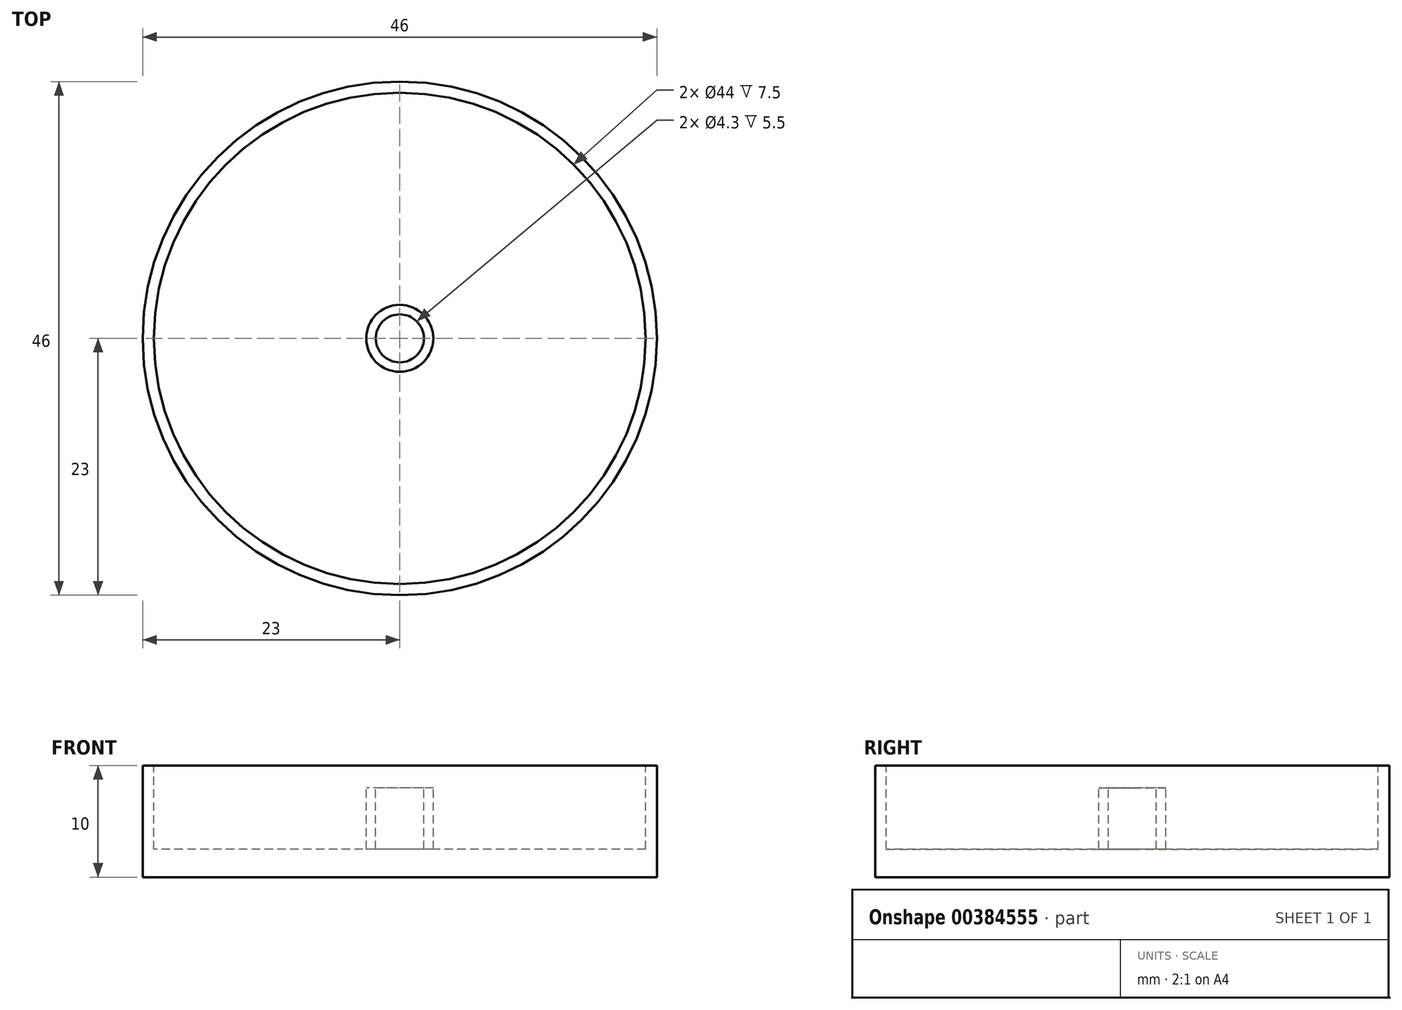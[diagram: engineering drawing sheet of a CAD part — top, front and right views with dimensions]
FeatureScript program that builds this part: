
annotation { "Feature Type Name" : "Feature", "Feature Type Description" : "" }
export const myFeature = defineFeature(function(context is Context, id is Id, definition is map)
    precondition{}
    {
        {
            var Q0;
            Q0=qCreatedBy(makeId("Top.planeOp"),FACE);
            var sketch = newSketch(context, id + "F0", { "sketchPlane" : qUnion([Q0])});
            skCircle(sketch, "E0", {"center": v(0, 0) * mm, "radius": 23 * mm});
            skSolve(sketch);
        }
        {
            var Q0;
            Q0 = qSketchRegion(id + "F0", true);
            extrude(context, id + "F1", {"entities" : qUnion([Q0]), "depth" : 10 * mm});
        }
        {
            var Q0;
            Q0=makeQuery(id+"F1.opExtrude","CAP_FACE",FACE,{"disambiguationData":[OSD([sQuery(id+"F0.wireOp",EDGE,"E0")])],"isStart":false});
            var sketch = newSketch(context, id + "F2", { "sketchPlane" : qUnion([Q0])});
            skCircle(sketch, "E1", {"center": v(0, 0) * mm, "radius": 22 * mm});
            skCircle(sketch, "E2", {"center": v(0, 0) * mm, "radius": 3 * mm});
            skCircle(sketch, "E3", {"center": v(0, 0) * mm, "radius": 2.15 * mm});
            skSolve(sketch);
        }
        {
            var Q0;
            Q0=makeQuery(id+"F2.imprint","IMPRINT",FACE,{"disambiguationData":[TD([[makeQuery(id+"F2.imprint","IMPRINT",EDGE,{"derivedFrom":sQuery(id+"F2.wireOp",EDGE,"E1")}),1.0]])]});
            var Q1;
            Q1=makeQuery(id+"F2.imprint","IMPRINT",FACE,{"disambiguationData":[TD([[makeQuery(id+"F2.imprint","IMPRINT",EDGE,{"derivedFrom":sQuery(id+"F2.wireOp",EDGE,"E3")}),1.0]])]});
            extrude(context, id + "F3", {"entities" : qUnion([Q0, Q1]), "operationType" : NewBodyOperationType.REMOVE, "oppositeDirection" : true, "depth" : 7.5 * mm});
        }
        {
            var Q0;
            Q0=makeQuery(id+"F3.boolean.opBoolean","SPLIT",FACE,{"disambiguationData":[TD([makeQuery(id+"F3.opExtrude","SWEPT_FACE",FACE,{"disambiguationData":[OSD([sQuery(id+"F2.wireOp",EDGE,"E2")])]})])],"derivedFrom":makeQuery(id+"F1.opExtrude","CAP_FACE",FACE,{"disambiguationData":[OSD([sQuery(id+"F0.wireOp",EDGE,"E0")])],"isStart":false})});
            extrude(context, id + "F4", {"entities" : qUnion([Q0]), "operationType" : NewBodyOperationType.REMOVE, "oppositeDirection" : true, "depth" : 2 * mm});
        }
    });
